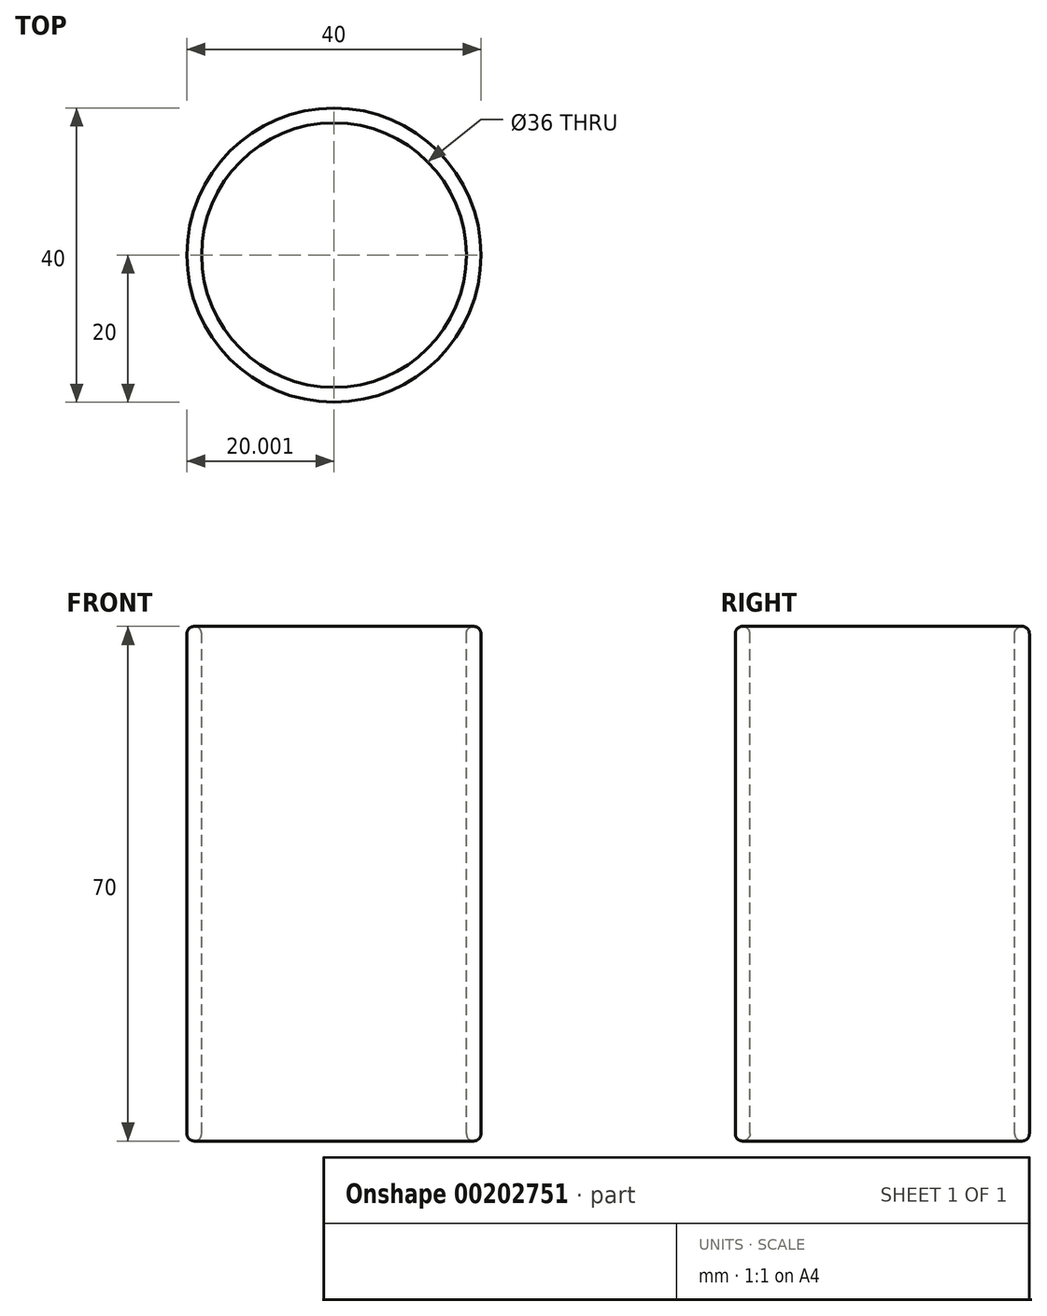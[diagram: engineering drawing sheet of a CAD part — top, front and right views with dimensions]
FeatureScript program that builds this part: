
annotation { "Feature Type Name" : "Feature", "Feature Type Description" : "" }
export const myFeature = defineFeature(function(context is Context, id is Id, definition is map)
    precondition{}
    {
        {
            var Q0;
            Q0=qCreatedBy(makeId("Front.planeOp"),FACE);
            var sketch = newSketch(context, id + "F0", { "sketchPlane" : qUnion([Q0])});
            skLineSegment(sketch, "E0.bottom", {"start": v(-8.9, 48.56) * mm, "end": v(-6.9, 48.56) * mm});
            skLineSegment(sketch, "E0.top", {"start": v(-8.9, -21.44) * mm, "end": v(-6.9, -21.44) * mm});
            skLineSegment(sketch, "E0.left", {"start": v(-8.9, 48.56) * mm, "end": v(-8.9, -21.44) * mm});
            skLineSegment(sketch, "E0.right", {"start": v(11.1, 48.56) * mm, "end": v(11.1, -21.44) * mm});
            skLineSegment(sketch, "E1.0", {"start": v(-6.9, 48.56) * mm, "end": v(-6.9, -21.44) * mm});
            skSolve(sketch);
        }
        {
            var Q0;
            Q0 = qSketchRegion(id + "F0", true);
            var Q1;
            Q1=sQuery(id+"F0.wireOp",EDGE,"E0.right");
            revolve(context, id + "F1", {"entities" : qUnion([Q0]), "axis" : qUnion([Q1]), "revolveType" : RevolveType.FULL});
        }
        {
            var Q0;
            Q0=makeQuery(id+"F1.opRevolve","SWEPT_FACE",FACE,{"disambiguationData":[OSD([sQuery(id+"F0.wireOp",EDGE,"E0.bottom")])]});
            var Q1;
            Q1=makeQuery(id+"F1.opRevolve","SWEPT_FACE",FACE,{"disambiguationData":[OSD([sQuery(id+"F0.wireOp",EDGE,"E0.top")])]});
            fillet(context, id + "F2", {"entities" : qUnion([Q0, Q1]), "radius" : 1 * mm, "tangentPropagation" : true, "allowEdgeOverflow" : false});
        }
    });
